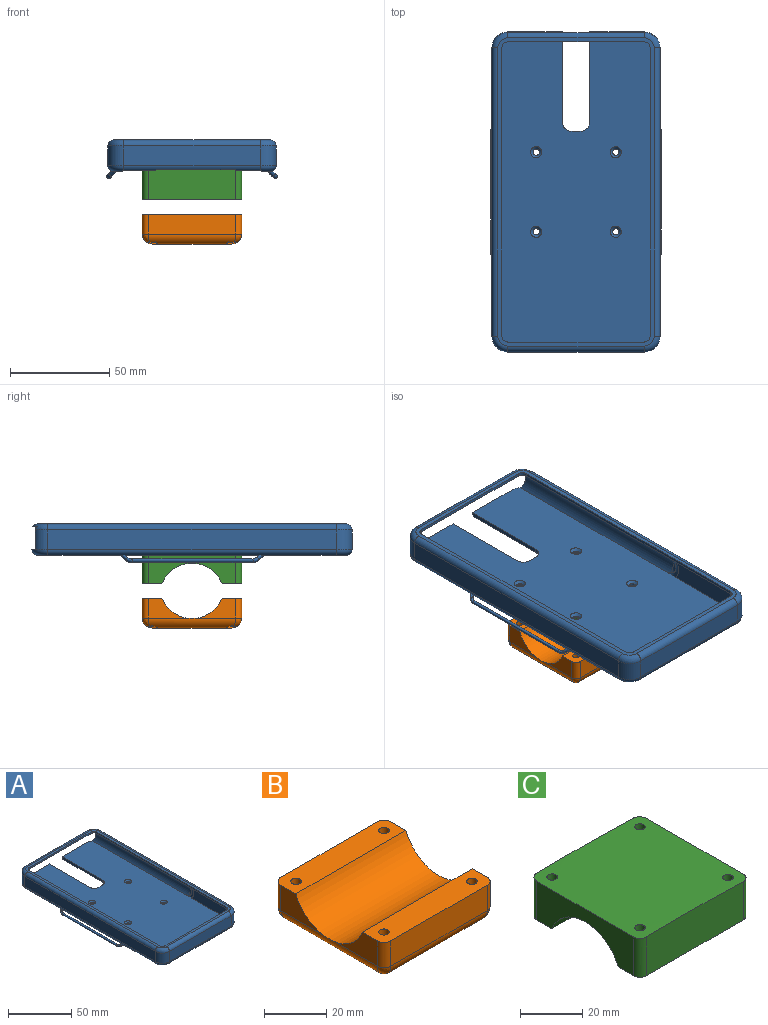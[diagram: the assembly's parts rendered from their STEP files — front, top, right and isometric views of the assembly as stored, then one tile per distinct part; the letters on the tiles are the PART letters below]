
ASSEMBLY  parts=3 mates=2
PART A: 71 faces, bbox 90.8x165x23.2 mm
  f0: cylinder r=750mm len=159.5mm, axis (0,1,0), area 11726.2mm2, adj f1,f33,f34,f35,f36,f37,f38,f39
  f1: cylinder r=3mm len=27.3mm, axis (-1,0,0), area 77.6mm2, adj f0,f21,f38,f48
  f2: cylinder r=8mm len=9.8mm, axis (0,0,1), area 52.9mm2, adj f3,f6,f38,f41
  f3: torus R=5mm, axis (0,0,1), area 41.7mm2, adj f2,f4,f11,f20,f32,f41
  f4: cylinder r=3mm len=68.6mm, axis (1,0,0), area 215.5mm2, adj f3,f11,f20,f28
  f5: plane 68.6x9.8mm, normal (0,-1,0), area 672.3mm2, adj f8,f10,f30,f37
  f6: plane 145x9.8mm, normal (1,0,0), area 1421mm2, adj f2,f8,f32,f40
  f7: plane 145x9.8mm, normal (-1,0,0), area 1421mm2, adj f9,f10,f27,f33
  f8: cylinder r=8mm len=9.8mm, axis (0,0,-1), area 123.2mm2, adj f5,f6,f31,f39
  f9: cylinder r=8mm len=9.8mm, axis (0,0,-1), area 70.2mm2, adj f7,f25,f28,f34
  f10: cylinder r=8mm len=9.8mm, axis (0,0,1), area 123.2mm2, adj f5,f7,f29,f35
  f11: plane 155x78.6mm, normal (0,0,1), area 904.7mm2, adj f3,f4,f12,f13,f14,f15,f16,f17
  f12: cylinder r=3mm len=3mm, axis (0,0,1), area 7.1mm2, adj f11,f13,f19,f20
  f13: plane 68.6x1.5mm, normal (0,-1,0), area 102.9mm2, adj f11,f12,f14,f20
  f14: cylinder r=3mm len=3mm, axis (0,0,1), area 7.1mm2, adj f11,f13,f15,f20
  f15: plane 145x1.5mm, normal (-1,0,0), area 217.5mm2, adj f11,f14,f16,f20
  f16: cylinder r=3mm len=3mm, axis (0,0,1), area 7.1mm2, adj f11,f15,f17,f20
  f17: plane 68.6x1.5mm, normal (0,1,0), area 102.9mm2, adj f11,f16,f18,f20
  f18: cylinder r=3mm len=3mm, axis (0,0,1), area 7.1mm2, adj f11,f17,f19,f20
  f19: plane 145x1.5mm, normal (1,0,0), area 217.5mm2, adj f11,f12,f18,f20
  f20: plane 160.24x81.41mm, normal (0,0,-1), area 1114.3mm2, adj f3,f4,f12,f13,f14,f15,f16,f17
  f21: plane 160.64x81.41mm, normal (0,0,1), area 11615.3mm2, adj f1,f22,f23,f24,f25,f26,f34,f36
  f22: cylinder r=5mm len=11.3mm, axis (0,0,-1), area 88.7mm2, adj f20,f21,f23,f26
  f23: plane 68.6x11.3mm, normal (0,1,0), area 775.2mm2, adj f20,f21,f22,f24
  f24: cylinder r=5mm len=11.3mm, axis (0,0,1), area 88.7mm2, adj f20,f21,f23,f25
  f25: plane 151.42x11.47mm, normal (1,0,0), area 1708.8mm2, adj f9,f20,f21,f24,f28
  f26: plane 41.06x11.31mm, normal (-1,0,0), area 446mm2, adj f20,f21,f22,f43
  f27: cylinder r=3mm len=145mm, axis (0,1,0), area 683.3mm2, adj f7,f11,f28,f29
  f28: torus R=5mm, axis (0,0,1), area 42.5mm2, adj f4,f9,f11,f20,f25,f27
  f29: torus R=5mm, axis (0,0,1), area 51.1mm2, adj f10,f11,f27,f30
  f30: cylinder r=3mm len=68.6mm, axis (-1,0,0), area 323.3mm2, adj f5,f11,f29,f31
  f31: torus R=5mm, axis (0,0,1), area 51.1mm2, adj f8,f11,f30,f32
  f32: cylinder r=3mm len=145mm, axis (0,-1,0), area 683.3mm2, adj f3,f6,f11,f31
  f33: cylinder r=3mm len=145mm, axis (0,-1,0), area 679.5mm2, adj f0,f7,f34,f35,f57,f58,f62
  f34: torus R=5mm, axis (0,0,1), area 46mm2, adj f0,f9,f21,f33,f36
  f35: torus R=5mm, axis (0,0,1), area 46mm2, adj f0,f10,f33,f37
  f36: cylinder r=3mm len=27.3mm, axis (-1,0,0), area 77.6mm2, adj f0,f21,f34,f44
  f37: cylinder r=3mm len=68.6mm, axis (1,0,0), area 174.5mm2, adj f0,f5,f35,f39
  f38: torus R=5mm, axis (0,0,1), area 46mm2, adj f0,f1,f2,f21,f40
  f39: torus R=5mm, axis (0,0,1), area 46mm2, adj f0,f8,f37,f40
  f40: cylinder r=3mm len=145mm, axis (0,1,0), area 679.9mm2, adj f0,f6,f38,f39,f50,f54,f55
  f41: cylinder r=10.5mm len=106.95mm, axis (0,1,0), area 1258.8mm2, adj f2,f3,f20,f21,f42,f43
  f42: torus R=5.5mm, axis (0,-1,0), area 22.1mm2, adj f41,f43
  f43: bspline ~13.92x9.56mm, area 48.5mm2, adj f20,f21,f26,f41,f42
  f44: plane 45x2mm, normal (1,0,0), area 89.6mm2, adj f0,f21,f36,f45
  f45: cylinder r=5mm len=5mm, axis (0,0,-1), area 15.6mm2, adj f0,f21,f44,f46
  f46: plane 4x1.97mm, normal (0,1,0), area 7.9mm2, adj f0,f21,f45,f47
  f47: cylinder r=5mm len=5mm, axis (0,0,-1), area 15.6mm2, adj f0,f21,f46,f48
  f48: plane 45x2mm, normal (-1,0,0), area 89.6mm2, adj f0,f1,f21,f47
  f49: bspline ~4.96x2.23mm, area 2.5mm2, adj f0,f50
  f50: bspline ~4.3x3.36mm, area 19.1mm2, adj f40,f49,f51
  f51: bspline ~5.58x3.58mm, area 14.8mm2, adj f50,f52
  f52: bspline ~63.35x3.58mm, area 339.2mm2, adj f51,f53
  f53: bspline ~4.92x4.92mm, area 14.8mm2, adj f52,f54
  f54: bspline ~3.92x3.92mm, area 17.4mm2, adj f0,f40,f53,f55
  f55: bspline ~5.28x5.28mm, area 3.5mm2, adj f0,f40,f54
  f56: bspline ~2.93x1.49mm, area 2.5mm2, adj f0,f62
  f57: bspline ~3.03x2.2mm, area 3.5mm2, adj f0,f33,f58
  f58: bspline ~3.92x3.92mm, area 17.4mm2, adj f0,f33,f57,f59
  f59: bspline ~4.92x4.92mm, area 14.8mm2, adj f58,f60
  f60: bspline ~63.35x3.58mm, area 339.2mm2, adj f59,f61
  f61: bspline ~5.58x3.58mm, area 14.8mm2, adj f60,f62
  f62: bspline ~4.3x3.36mm, area 18.5mm2, adj f33,f56,f61
  f63: cylinder r=1.6mm len=3.2mm, axis (0,0,1), area 10.4mm2, adj f0,f64
  f64: cone r=1.6mm half-angle=46deg, axis (0,0,1), area 23.1mm2, adj f21,f63
  f65: cylinder r=1.6mm len=3.2mm, axis (0,0,1), area 11.3mm2, adj f0,f66
  f66: cone r=1.6mm half-angle=46deg, axis (0,0,1), area 23.1mm2, adj f21,f65
  f67: cylinder r=1.6mm len=3.2mm, axis (0,0,1), area 11.3mm2, adj f0,f68
  f68: cone r=1.6mm half-angle=46deg, axis (0,0,1), area 23.1mm2, adj f21,f67
  f69: cylinder r=1.6mm len=3.2mm, axis (0,0,1), area 10.4mm2, adj f0,f70
  f70: cone r=1.6mm half-angle=46deg, axis (0,0,1), area 23.1mm2, adj f21,f69
PART B: 54 faces, bbox 50.3x50.3x15.3 mm
  f0: plane 19.16x10mm, normal (1,0,0), area 108.3mm2, adj f7,f13,f16,f46
  f1: plane 19.16x10mm, normal (-1,0,0), area 108.3mm2, adj f12,f13,f14,f53
  f2: plane 40x40mm, normal (0,0,-1), area 1571.4mm2, adj f19,f20,f27,f28,f36,f37,f40,f45
  f3: cylinder r=1.7mm len=5mm, axis (0,0,-1), area 53.4mm2, adj f7,f39
  f4: cylinder r=1.7mm len=5mm, axis (0,0,-1), area 53.4mm2, adj f7,f32
  f5: cylinder r=1.7mm len=5mm, axis (0,0,-1), area 53.4mm2, adj f12,f25
  f6: cylinder r=1.7mm len=5mm, axis (0,0,-1), area 53.4mm2, adj f12,f18
  f7: plane 50x9.9mm, normal (0,0,1), area 472.9mm2, adj f0,f3,f4,f9,f10,f13,f15,f16
  f8: plane 44x10mm, normal (0,1,0), area 440mm2, adj f12,f14,f17,f49
  f9: plane 19.16x10mm, normal (-1,0,0), area 108.3mm2, adj f7,f13,f15,f53
  f10: plane 44x10mm, normal (0,-1,0), area 440mm2, adj f7,f15,f16,f50
  f11: plane 19.16x10mm, normal (1,0,0), area 108.3mm2, adj f12,f13,f17,f46
  f12: plane 50x9.9mm, normal (0,0,1), area 472.9mm2, adj f1,f5,f6,f8,f11,f13,f14,f17
  f13: cylinder r=16.25mm len=50mm, axis (1,0,0), area 1938mm2, adj f0,f1,f7,f9,f11,f12,f46,f53
  f14: cylinder r=3mm len=10mm, axis (0,0,1), area 47.1mm2, adj f1,f8,f12,f51
  f15: cylinder r=3mm len=10mm, axis (0,0,-1), area 47.1mm2, adj f7,f9,f10,f52
  f16: cylinder r=3mm len=10mm, axis (0,0,1), area 47.1mm2, adj f0,f7,f10,f48
  f17: cylinder r=3mm len=10mm, axis (0,0,-1), area 47.1mm2, adj f8,f11,f12,f47
  f18: plane 6.64x5.75mm, normal (0,0,-1), area 19.6mm2, adj f6,f19,f20,f21,f22,f23,f24
  f19: plane 10x2.88mm, normal (-0.87,0.5,0), area 33.2mm2, adj f2,f18,f20,f24
  f20: plane 10x3.32mm, normal (0,1,0), area 33mm2, adj f2,f18,f19,f21,f53
  f21: plane 9.88x3.04mm, normal (0.87,0.5,0), area 30.9mm2, adj f18,f20,f22,f53
  f22: plane 9.63x3.16mm, normal (0.87,-0.5,0), area 30.4mm2, adj f18,f21,f23,f51,f53
  f23: plane 9.12x3.35mm, normal (0,-1,0), area 30.2mm2, adj f18,f22,f24,f49,f51
  f24: plane 10.08x2.96mm, normal (-0.87,-0.5,0), area 32.2mm2, adj f18,f19,f23,f49
  f25: plane 6.64x5.75mm, normal (0,0,-1), area 19.6mm2, adj f5,f26,f27,f28,f29,f30,f31
  f26: plane 9.88x3.04mm, normal (-0.87,0.5,0), area 30.9mm2, adj f25,f27,f31,f46
  f27: plane 10x3.32mm, normal (0,1,0), area 33mm2, adj f2,f25,f26,f28,f46
  f28: plane 10x2.88mm, normal (0.87,0.5,0), area 33.2mm2, adj f2,f25,f27,f29
  f29: plane 10.08x2.96mm, normal (0.87,-0.5,0), area 32.2mm2, adj f25,f28,f30,f49
  f30: plane 9.13x3.36mm, normal (0,-1,0), area 30.2mm2, adj f25,f29,f31,f47,f49
  f31: plane 9.63x3.16mm, normal (-0.87,-0.5,0), area 30.4mm2, adj f25,f26,f30,f46,f47
  f32: plane 6.64x5.75mm, normal (0,0,-1), area 19.6mm2, adj f4,f33,f34,f35,f36,f37,f38
  f33: plane 9.63x3.16mm, normal (-0.87,0.5,0), area 30.4mm2, adj f32,f34,f38,f46,f48
  f34: plane 9.12x3.35mm, normal (0,1,0), area 30.2mm2, adj f32,f33,f35,f48,f50
  f35: plane 10.08x2.96mm, normal (0.87,0.5,0), area 32.2mm2, adj f32,f34,f36,f50
  f36: plane 10x2.88mm, normal (0.87,-0.5,0), area 33.2mm2, adj f2,f32,f35,f37
  f37: plane 10x3.32mm, normal (0,-1,0), area 33mm2, adj f2,f32,f36,f38,f46
  f38: plane 9.88x3.04mm, normal (-0.87,-0.5,0), area 30.9mm2, adj f32,f33,f37,f46
  f39: plane 6.64x5.75mm, normal (0,0,-1), area 19.6mm2, adj f3,f40,f41,f42,f43,f44,f45
  f40: plane 10x2.88mm, normal (-0.87,-0.5,0), area 33.2mm2, adj f2,f39,f41,f45
  f41: plane 10.08x2.96mm, normal (-0.87,0.5,0), area 32.2mm2, adj f39,f40,f42,f50
  f42: plane 9.13x3.36mm, normal (0,1,0), area 30.2mm2, adj f39,f41,f43,f50,f52
  f43: plane 9.63x3.16mm, normal (0.87,0.5,0), area 30.4mm2, adj f39,f42,f44,f52,f53
  f44: plane 9.88x3.04mm, normal (0.87,-0.5,0), area 30.9mm2, adj f39,f43,f45,f53
  f45: plane 10x3.32mm, normal (0,-1,0), area 33mm2, adj f2,f39,f40,f44,f53
  f46: cylinder r=5mm len=44mm, axis (0,1,0), area 312.5mm2, adj f0,f2,f11,f13,f26,f27,f31,f33
  f47: bspline ~5.04x4.12mm, area 20.4mm2, adj f17,f30,f31,f46,f49
  f48: bspline ~5.04x4.12mm, area 20.4mm2, adj f16,f33,f34,f46,f50
  f49: cylinder r=5mm len=44mm, axis (-1,0,0), area 314mm2, adj f2,f8,f23,f24,f29,f30,f47,f51
  f50: cylinder r=5mm len=44mm, axis (1,0,0), area 314mm2, adj f2,f10,f34,f35,f41,f42,f48,f52
  f51: bspline ~5.04x4.12mm, area 20.4mm2, adj f14,f22,f23,f49,f53
  f52: bspline ~5.04x4.12mm, area 20.4mm2, adj f15,f42,f43,f50,f53
  f53: cylinder r=5mm len=44mm, axis (0,-1,0), area 312.5mm2, adj f1,f2,f9,f13,f20,f21,f22,f43
PART C: 16 faces, bbox 50x50x15.6 mm
  f0: plane 44x15mm, normal (1,0,0), area 435.7mm2, adj f1,f2,f4,f7,f13,f15
  f1: plane 50x9.9mm, normal (0,0,-1), area 472.9mm2, adj f0,f3,f6,f7,f8,f11,f12,f13
  f2: cylinder r=750mm len=50mm, axis (0,1,0), area 2456.5mm2, adj f0,f3,f5,f6,f8,f9,f10,f11
  f3: plane 44x15.27mm, normal (-1,0,0), area 447.4mm2, adj f1,f2,f4,f7,f12,f14
  f4: plane 50x9.9mm, normal (0,0,-1), area 472.9mm2, adj f0,f3,f5,f7,f9,f10,f14,f15
  f5: plane 44x15.56mm, normal (0,-1,0), area 679.5mm2, adj f2,f4,f14,f15
  f6: plane 44x15.56mm, normal (0,1,0), area 679.5mm2, adj f1,f2,f12,f13
  f7: cylinder r=16.25mm len=50mm, axis (1,0,0), area 1938mm2, adj f0,f1,f3,f4
  f8: cylinder r=1.7mm len=15.42mm, axis (0,0,-1), area 164.4mm2, adj f1,f2
  f9: cylinder r=1.7mm len=15.23mm, axis (0,0,-1), area 162.1mm2, adj f2,f4
  f10: cylinder r=1.7mm len=15.42mm, axis (0,0,-1), area 164.4mm2, adj f2,f4
  f11: cylinder r=1.7mm len=15.23mm, axis (0,0,-1), area 162.1mm2, adj f1,f2
  f12: cylinder r=3mm len=15.35mm, axis (0,0,-1), area 72.1mm2, adj f1,f2,f3,f6
  f13: cylinder r=3mm len=15.11mm, axis (0,0,1), area 70.9mm2, adj f0,f1,f2,f6
  f14: cylinder r=3mm len=15.35mm, axis (0,0,1), area 72.1mm2, adj f2,f3,f4,f5
  f15: cylinder r=3mm len=15.11mm, axis (0,0,-1), area 70.9mm2, adj f0,f2,f4,f5
PLACE A rot(axis=(-0.42,-0.49,0.76),0deg) t=(-37.74,-35.6,13.03)mm
PLACE B t=(-37.74,-35.6,-23.51)mm
PLACE C t=(-41.47,-10.6,-10.73)mm
MATE slider C.f8 <-> B.f6  axis (0,0,-1) through (-57.74,-15.6,-1.21)mm
MATE fastened A.f63 <-> C.f8  axis (0,0,1) through (-57.74,-15.6,14.31)mm
